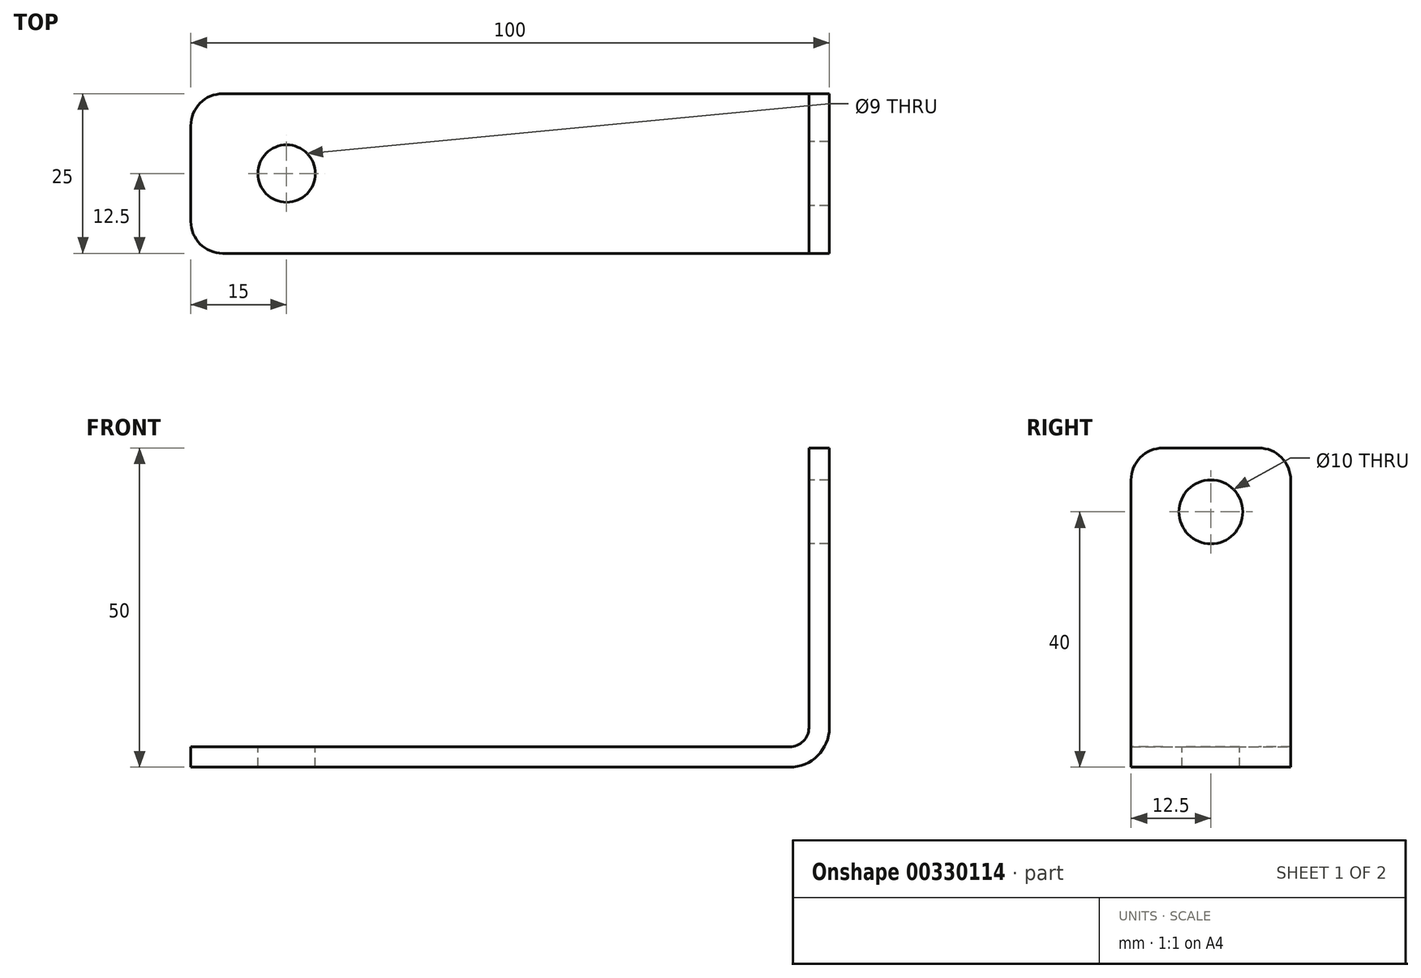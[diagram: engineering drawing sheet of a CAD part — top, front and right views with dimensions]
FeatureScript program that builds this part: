
annotation { "Feature Type Name" : "Feature", "Feature Type Description" : "" }
export const myFeature = defineFeature(function(context is Context, id is Id, definition is map)
    precondition{}
    {
        {
            var Q0;
            Q0=qCreatedBy(makeId("Front.planeOp"),FACE);
            var sketch = newSketch(context, id + "F0", { "sketchPlane" : qUnion([Q0])});
            skLineSegment(sketch, "E0.bottom", {"start": v(0, 0) * mm, "end": v(93.8, 0) * mm});
            skLineSegment(sketch, "E1", {"start": v(100, 6.2) * mm, "end": v(100, 50) * mm});
            skPoint(sketch, "E2.visualSharp", {"position": v(100, 0) * mm});
            skArc(sketch, "E2.filletArc", {"start": v(93.8, 0) * mm, "mid": v(98.18, 1.82) * mm, "end": v(100, 6.2) * mm});
            skLineSegment(sketch, "E3.0", {"start": v(96.8, 6.2) * mm, "end": v(96.8, 50) * mm});
            skLineSegment(sketch, "E3.1", {"start": v(0, 3.2) * mm, "end": v(93.8, 3.2) * mm});
            skLineSegment(sketch, "E4", {"start": v(96.8, 50) * mm, "end": v(100, 50) * mm});
            skLineSegment(sketch, "E5", {"start": v(0, 0) * mm, "end": v(0, 3.2) * mm});
            skPoint(sketch, "E6.visualSharp", {"position": v(96.8, 3.2) * mm});
            skArc(sketch, "E6.filletArc", {"start": v(93.8, 3.2) * mm, "mid": v(95.92, 4.08) * mm, "end": v(96.8, 6.2) * mm});
            skSolve(sketch);
        }
        {
            var Q0;
            Q0 = qSketchRegion(id + "F0", true);
            extrude(context, id + "F1", {"entities" : qUnion([Q0]), "depth" : 25 * mm});
        }
        {
            var Q0;
            Q0=makeQuery(id+"F1.opExtrude","SWEPT_FACE",FACE,{"disambiguationData":[OSD([sQuery(id+"F0.wireOp",EDGE,"E3.0")])]});
            var sketch = newSketch(context, id + "F2", { "sketchPlane" : qUnion([Q0])});
            skCircle(sketch, "E7", {"center": v(12.5, 40) * mm, "radius": 5 * mm});
            skSolve(sketch);
        }
        {
            var Q0;
            Q0 = qSketchRegion(id + "F2", true);
            extrude(context, id + "F3", {"entities" : qUnion([Q0]), "operationType" : NewBodyOperationType.REMOVE, "endBound" : BoundingType.SYMMETRIC, "oppositeDirection" : true, "depth" : 25 * mm});
        }
        {
            var Q0;
            Q0=makeQuery(id+"F1.opExtrude","SWEPT_FACE",FACE,{"disambiguationData":[OSD([sQuery(id+"F0.wireOp",EDGE,"E3.1")])]});
            var sketch = newSketch(context, id + "F4", { "sketchPlane" : qUnion([Q0])});
            skCircle(sketch, "E8", {"center": v(15, -12.5) * mm, "radius": 4.5 * mm});
            skSolve(sketch);
        }
        {
            var Q0;
            Q0 = qSketchRegion(id + "F4", true);
            extrude(context, id + "F5", {"entities" : qUnion([Q0]), "operationType" : NewBodyOperationType.REMOVE, "endBound" : BoundingType.THROUGH_ALL, "oppositeDirection" : true, "depth" : 25 * mm});
        }
        {
            var Q0;
            Q0=makeQuery(id+"F1.opExtrude","CAP_EDGE",EDGE,{"disambiguationData":[OSD([sQuery(id+"F0.wireOp",EDGE,"E5")])],"isStart":false});
            var Q1;
            Q1=makeQuery(id+"F1.opExtrude","CAP_EDGE",EDGE,{"disambiguationData":[OSD([sQuery(id+"F0.wireOp",EDGE,"E5")])],"isStart":true});
            var Q2;
            Q2=makeQuery(id+"F1.opExtrude","CAP_EDGE",EDGE,{"disambiguationData":[OSD([sQuery(id+"F0.wireOp",EDGE,"E4")])],"isStart":true});
            var Q3;
            Q3=makeQuery(id+"F1.opExtrude","CAP_EDGE",EDGE,{"disambiguationData":[OSD([sQuery(id+"F0.wireOp",EDGE,"E4")])],"isStart":false});
            fillet(context, id + "F6", {"entities" : qUnion([Q0, Q1, Q2, Q3]), "radius" : 5 * mm, "tangentPropagation" : true, "allowEdgeOverflow" : false});
        }
    });
